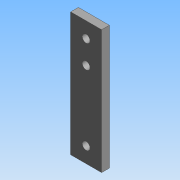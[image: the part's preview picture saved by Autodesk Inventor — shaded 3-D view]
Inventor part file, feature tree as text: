
AUTODESK INVENTOR PART (.ipt)
format: ipt  version: 2015 (Build 190159000, 159)  size: 92,672 bytes
history: native  units: mm
features: extrude x2, projected_geometry x1
ambient origin geometry x8: Origin, YZ Plane, XZ Plane, XY Plane, X Axis, Y Axis, Z Axis, Center Point
bodies: Solid1 (feature_tree)
feature tree (3):
  extrude  "Extrusion1"  Depth=80.0mm
  extrude  "Extrusion3"  Depth=5.0mm TaperAngle=0.0deg
  projected_geometry  "Projected Loop1"
